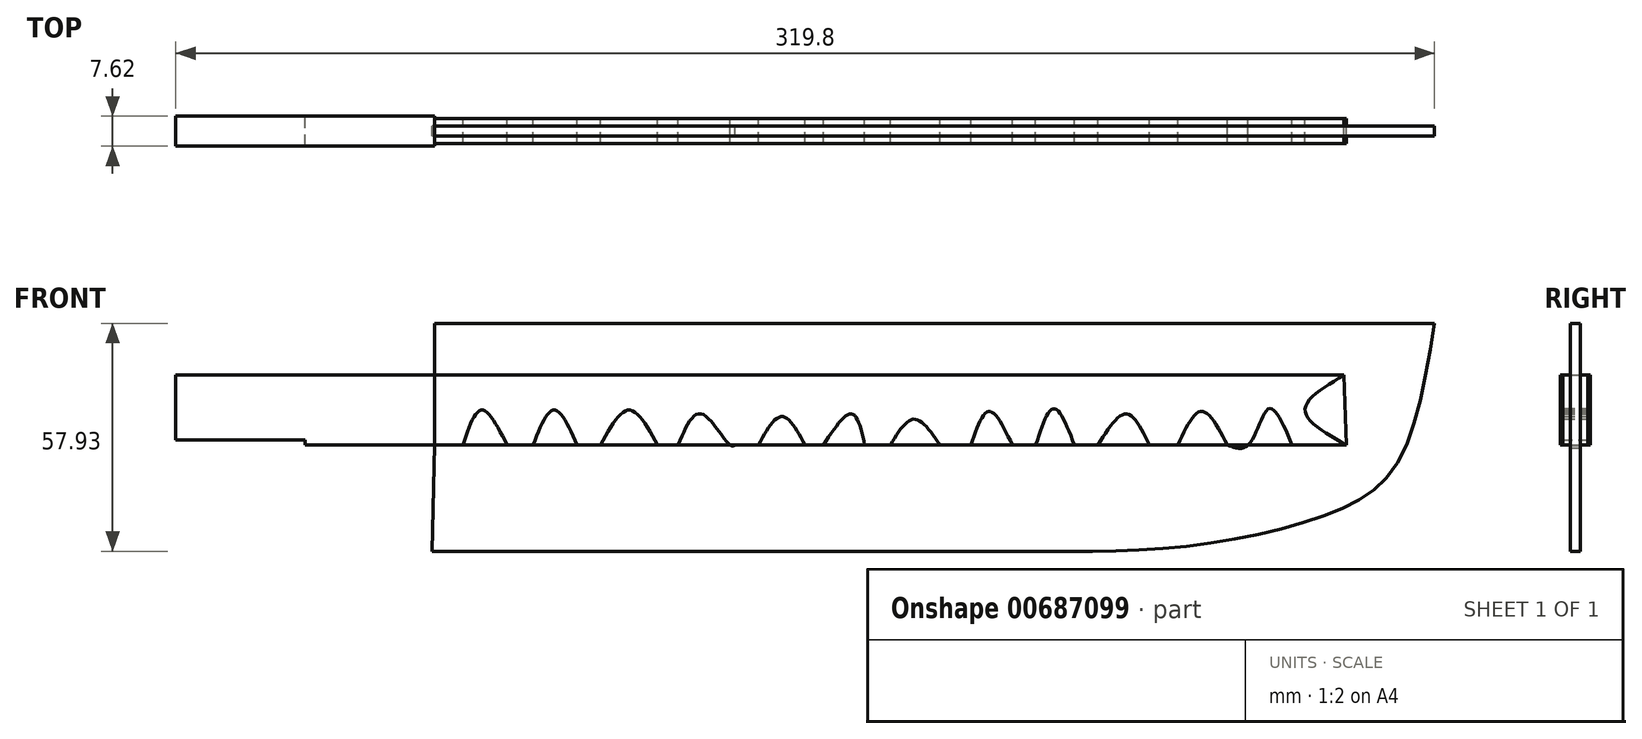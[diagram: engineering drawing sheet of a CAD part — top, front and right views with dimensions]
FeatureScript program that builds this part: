
annotation { "Feature Type Name" : "Feature", "Feature Type Description" : "" }
export const myFeature = defineFeature(function(context is Context, id is Id, definition is map)
    precondition{}
    {
        {
            var Q0;
            Q0=qCreatedBy(makeId("Front.planeOp"),FACE);
            var sketch = newSketch(context, id + "F0", { "sketchPlane" : qUnion([Q0])});
            skLineSegment(sketch, "E0.bottom", {"start": v(-276.04, 41.9) * mm, "end": v(-243.14, 41.9) * mm});
            skLineSegment(sketch, "E0.top", {"start": v(-276.04, 25.45) * mm, "end": v(-243.14, 25.45) * mm});
            skLineSegment(sketch, "E0.left", {"start": v(-276.04, 41.9) * mm, "end": v(-276.04, 25.45) * mm});
            skLineSegment(sketch, "E0.right", {"start": v(-243.14, 41.9) * mm, "end": v(-243.14, 25.45) * mm});
            skLineSegment(sketch, "E1.bottom", {"start": v(-243.14, 41.9) * mm, "end": v(-210.24, 41.9) * mm});
            skLineSegment(sketch, "E1.top", {"start": v(-243.14, 24.13) * mm, "end": v(-210.24, 24.13) * mm});
            skLineSegment(sketch, "E1.left", {"start": v(-243.14, 41.9) * mm, "end": v(-243.14, 24.13) * mm});
            skLineSegment(sketch, "E1.right", {"start": v(-210.24, 41.9) * mm, "end": v(-210.24, 24.13) * mm});
            skLineSegment(sketch, "E2", {"start": v(-259.59, 41.9) * mm, "end": v(-270.12, 25.45) * mm});
            skLineSegment(sketch, "E3", {"start": v(-250.38, 41.9) * mm, "end": v(-259.59, 25.45) * mm});
            skLineSegment(sketch, "E4", {"start": v(-226.69, 41.9) * mm, "end": v(-243.14, 25.45) * mm});
            skLineSegment(sketch, "E5", {"start": v(-218.79, 41.9) * mm, "end": v(-233.27, 24.13) * mm});
            skLineSegment(sketch, "E6", {"start": v(-210.24, 33.02) * mm, "end": v(-220.76, 24.13) * mm});
            skLineSegment(sketch, "E7", {"start": v(-210.24, 41.9) * mm, "end": v(-210.24, 55.06) * mm});
            skLineSegment(sketch, "E8", {"start": v(-210.24, 55.06) * mm, "end": v(43.76, 55.06) * mm});
            skFitSpline(sketch, "E9", {"points": [v(43.76, 55.06) * mm, v(33.9, 18.87) * mm, v(16.13, 6.37) * mm, v(-18.75, -1.53) * mm, v(-54.94, -2.85) * mm], "startDerivative": vector(-24.9, -154.88) * mm, "endDerivative": vector(-135.33, 0.6) * mm});
            skLineSegment(sketch, "E10", {"start": v(-54.94, -2.85) * mm, "end": v(-210.9, -2.85) * mm});
            skLineSegment(sketch, "E11", {"start": v(-210.24, 24.13) * mm, "end": v(-210.9, -2.85) * mm});
            skLineSegment(sketch, "E12", {"start": v(-210.24, 41.9) * mm, "end": v(20.73, 41.9) * mm});
            skLineSegment(sketch, "E13", {"start": v(-210.24, 24.13) * mm, "end": v(21.4, 24.13) * mm});
            skLineSegment(sketch, "E14", {"start": v(20.73, 41.9) * mm, "end": v(21.4, 24.13) * mm});
            skFitSpline(sketch, "E15", {"points": [v(-203, 24.13) * mm, v(-198.4, 33.02) * mm, v(-191.81, 24.13) * mm], "startDerivative": vector(8.62, 26.89) * mm, "endDerivative": vector(13.71, -26.45) * mm});
            skFitSpline(sketch, "E16", {"points": [v(-185.23, 24.13) * mm, v(-179.97, 33.02) * mm, v(-174.04, 24.13) * mm], "startDerivative": vector(10.34, 26.73) * mm, "endDerivative": vector(12.03, -26.58) * mm});
            skFitSpline(sketch, "E17", {"points": [v(-168.12, 24.13) * mm, v(-160.88, 33.02) * mm, v(-153.64, 24.13) * mm], "startDerivative": vector(14.48, 26.65) * mm, "endDerivative": vector(14.48, -26.65) * mm});
            skFitSpline(sketch, "E18", {"points": [v(-148.38, 24.13) * mm, v(-142.46, 32.03) * mm, v(-135.22, 24.13) * mm, v(-133.9, 24.13) * mm], "startDerivative": vector(12.78, 30.9) * mm, "endDerivative": vector(7.43, 3.98) * mm});
            skFitSpline(sketch, "E19", {"points": [v(-127.98, 24.13) * mm, v(-122.06, 31.37) * mm, v(-116.14, 24.13) * mm], "startDerivative": vector(11.84, 21.72) * mm, "endDerivative": vector(11.84, -21.72) * mm});
            skFitSpline(sketch, "E20", {"points": [v(-111.53, 24.13) * mm, v(-104.3, 32.03) * mm, v(-101, 24.13) * mm], "startDerivative": vector(15.49, 23.32) * mm, "endDerivative": vector(5.38, -24.2) * mm});
            skFitSpline(sketch, "E21", {"points": [v(-94.42, 24.13) * mm, v(-88.5, 30.71) * mm, v(-81.92, 24.13) * mm], "startDerivative": vector(11.75, 19.83) * mm, "endDerivative": vector(13.25, -19.66) * mm});
            skFitSpline(sketch, "E22", {"points": [v(-74.02, 24.13) * mm, v(-69.42, 32.69) * mm, v(-63.5, 24.13) * mm], "startDerivative": vector(8.81, 25.82) * mm, "endDerivative": vector(12.22, -25.52) * mm});
            skFitSpline(sketch, "E23", {"points": [v(-57.57, 24.13) * mm, v(-52.97, 33.34) * mm, v(-47.7, 24.13) * mm], "startDerivative": vector(9, 27.7) * mm, "endDerivative": vector(10.75, -27.57) * mm});
            skFitSpline(sketch, "E24", {"points": [v(-41.78, 24.13) * mm, v(-34.54, 32.03) * mm, v(-28.62, 24.13) * mm], "startDerivative": vector(14.72, 23.54) * mm, "endDerivative": vector(11.58, -23.86) * mm});
            skFitSpline(sketch, "E25", {"points": [v(-21.38, 24.13) * mm, v(-15.46, 32.69) * mm, v(-8.88, 24.13) * mm], "startDerivative": vector(11.68, 25.74) * mm, "endDerivative": vector(13.32, -25.59) * mm});
            skFitSpline(sketch, "E26", {"points": [v(-8.88, 24.13) * mm, v(-3.61, 24.13) * mm, v(1.65, 33.34) * mm, v(7.57, 24.13) * mm], "startDerivative": vector(21.76, -8.33) * mm, "endDerivative": vector(16.75, -40.18) * mm});
            skPoint(sketch, "E27.1.internal.snap0", {"position": v(21.06, 33.02) * mm});
            skFitSpline(sketch, "E27", {"points": [v(21.4, 24.13) * mm, v(10.86, 33.02) * mm, v(20.73, 41.9) * mm], "startDerivative": vector(-31.16, 17.52) * mm, "endDerivative": vector(30.03, 18.01) * mm});
            skSolve(sketch);
        }
        {
            var Q0;
            Q0=makeQuery(id+"F0.imprint","IMPRINT",FACE,{"disambiguationData":[TD([[makeQuery(id+"F0.imprint","IMPRINT",EDGE,{"derivedFrom":sQuery(id+"F0.wireOp",EDGE,"E7")}),-1.0]])]});
            extrude(context, id + "F1", {"entities" : qUnion([Q0]), "endBound" : BoundingType.SYMMETRIC, "depth" : 2.54 * mm, "offsetDistance" : 25.4 * mm});
        }
        {
            var Q0;
            {var subQ0=sQuery(id+"F0.wireOp",EDGE,"E0.left");Q0=makeQuery(id+"F0.imprint","IMPRINT",FACE,{"disambiguationData":[TD([[makeQuery(id+"F0.imprint","IMPRINT",EDGE,{"derivedFrom":subQ0}),1.0]])]});}
            var Q1;
            {var subQ0=sQuery(id+"F0.wireOp",EDGE,"E2");Q1=makeQuery(id+"F0.imprint","IMPRINT",FACE,{"disambiguationData":[TD([[makeQuery(id+"F0.imprint","IMPRINT",EDGE,{"derivedFrom":subQ0}),1.0]])]});}
            var Q2;
            {var subQ3=sQuery(id+"F0.wireOp",EDGE,"E3");Q2=makeQuery(id+"F0.imprint","IMPRINT",FACE,{"disambiguationData":[TD([[makeQuery(id+"F0.imprint","IMPRINT",EDGE,{"derivedFrom":subQ3}),1.0]])]});}
            var Q3;
            {var subQ3=sQuery(id+"F0.wireOp",EDGE,"E4");Q3=makeQuery(id+"F0.imprint","IMPRINT",FACE,{"disambiguationData":[TD([[makeQuery(id+"F0.imprint","IMPRINT",EDGE,{"derivedFrom":subQ3}),-1.0]])]});}
            var Q4;
            {var subQ0=sQuery(id+"F0.wireOp",EDGE,"E4");Q4=makeQuery(id+"F0.imprint","IMPRINT",FACE,{"disambiguationData":[TD([[makeQuery(id+"F0.imprint","IMPRINT",EDGE,{"derivedFrom":subQ0}),1.0]])]});}
            var Q5;
            {var subQ0=sQuery(id+"F0.wireOp",EDGE,"E5");Q5=makeQuery(id+"F0.imprint","IMPRINT",FACE,{"disambiguationData":[TD([[makeQuery(id+"F0.imprint","IMPRINT",EDGE,{"derivedFrom":subQ0}),1.0]])]});}
            var Q6;
            {var subQ3=sQuery(id+"F0.wireOp",EDGE,"E6");Q6=makeQuery(id+"F0.imprint","IMPRINT",FACE,{"disambiguationData":[TD([[makeQuery(id+"F0.imprint","IMPRINT",EDGE,{"derivedFrom":subQ3}),1.0]])]});}
            extrude(context, id + "F2", {"entities" : qUnion([Q0, Q1, Q2, Q3, Q4, Q5, Q6]), "endBound" : BoundingType.SYMMETRIC, "depth" : 7.62 * mm, "offsetDistance" : 25.4 * mm});
        }
        {
            var Q0;
            {var subQ16=sQuery(id+"F0.wireOp",EDGE,"E12");Q0=makeQuery(id+"F0.imprint","IMPRINT",FACE,{"disambiguationData":[TD([[makeQuery(id+"F0.imprint","IMPRINT",EDGE,{"derivedFrom":subQ16}),-1.0]])]});}
            extrude(context, id + "F3", {"entities" : qUnion([Q0]), "endBound" : BoundingType.SYMMETRIC, "depth" : 6.35 * mm, "offsetDistance" : 25.4 * mm});
        }
        {
            var Q0;
            Q0=sQuery(id+"F0.wireOp",EDGE,"E15");
            var Q1;
            Q1=sQuery(id+"F0.wireOp",EDGE,"E16");
            var Q2;
            Q2=sQuery(id+"F0.wireOp",EDGE,"E17");
            var Q3;
            Q3=sQuery(id+"F0.wireOp",EDGE,"E18");
            var Q4;
            Q4=sQuery(id+"F0.wireOp",EDGE,"E19");
            var Q5;
            Q5=sQuery(id+"F0.wireOp",EDGE,"E20");
            var Q6;
            Q6=sQuery(id+"F0.wireOp",EDGE,"E21");
            var Q7;
            Q7=sQuery(id+"F0.wireOp",EDGE,"E22");
            var Q8;
            Q8=sQuery(id+"F0.wireOp",EDGE,"E23");
            var Q9;
            Q9=sQuery(id+"F0.wireOp",EDGE,"E24");
            var Q10;
            Q10=sQuery(id+"F0.wireOp",EDGE,"E25");
            var Q11;
            Q11=sQuery(id+"F0.wireOp",EDGE,"E26");
            var Q12;
            Q12=sQuery(id+"F0.wireOp",EDGE,"E27");
            extrude(context, id + "F4", {"bodyType" : ToolBodyType.SURFACE, "surfaceEntities" : qUnion([Q0, Q1, Q2, Q3, Q4, Q5, Q6, Q7, Q8, Q9, Q10, Q11, Q12]), "endBound" : BoundingType.SYMMETRIC, "depth" : 6.35 * mm, "offsetDistance" : 25.4 * mm});
        }
        {
            var Q0;
            Q0=qCreatedBy(makeId("Front.planeOp"),FACE);
            var sketch = newSketch(context, id + "F5", { "sketchPlane" : qUnion([Q0])});
            skFitSpline(sketch, "E28", {"points": [v(-276.05, 25.22) * mm, v(-278.78, 13.1) * mm, v(-273.7, 0) * mm, v(-268.62, -14.27) * mm, v(-270.97, -25.22) * mm, v(-283.87, -26) * mm, v(-283.08, -8.8) * mm, v(-290.51, 3.71) * mm, v(-290.9, 25.6) * mm, v(-277.22, 37.73) * mm], "startDerivative": vector(-46.06, -120.27) * mm, "endDerivative": vector(134.56, 77.6) * mm});
            skSolve(sketch);
        }
        {
            var Q0;
            Q0=sQuery(id+"F5.wireOp",EDGE,"E28");
            extrude(context, id + "F6", {"bodyType" : ToolBodyType.SURFACE, "surfaceEntities" : qUnion([Q0]), "depth" : 1.78 * mm, "offsetDistance" : 25.4 * mm});
        }
    });
